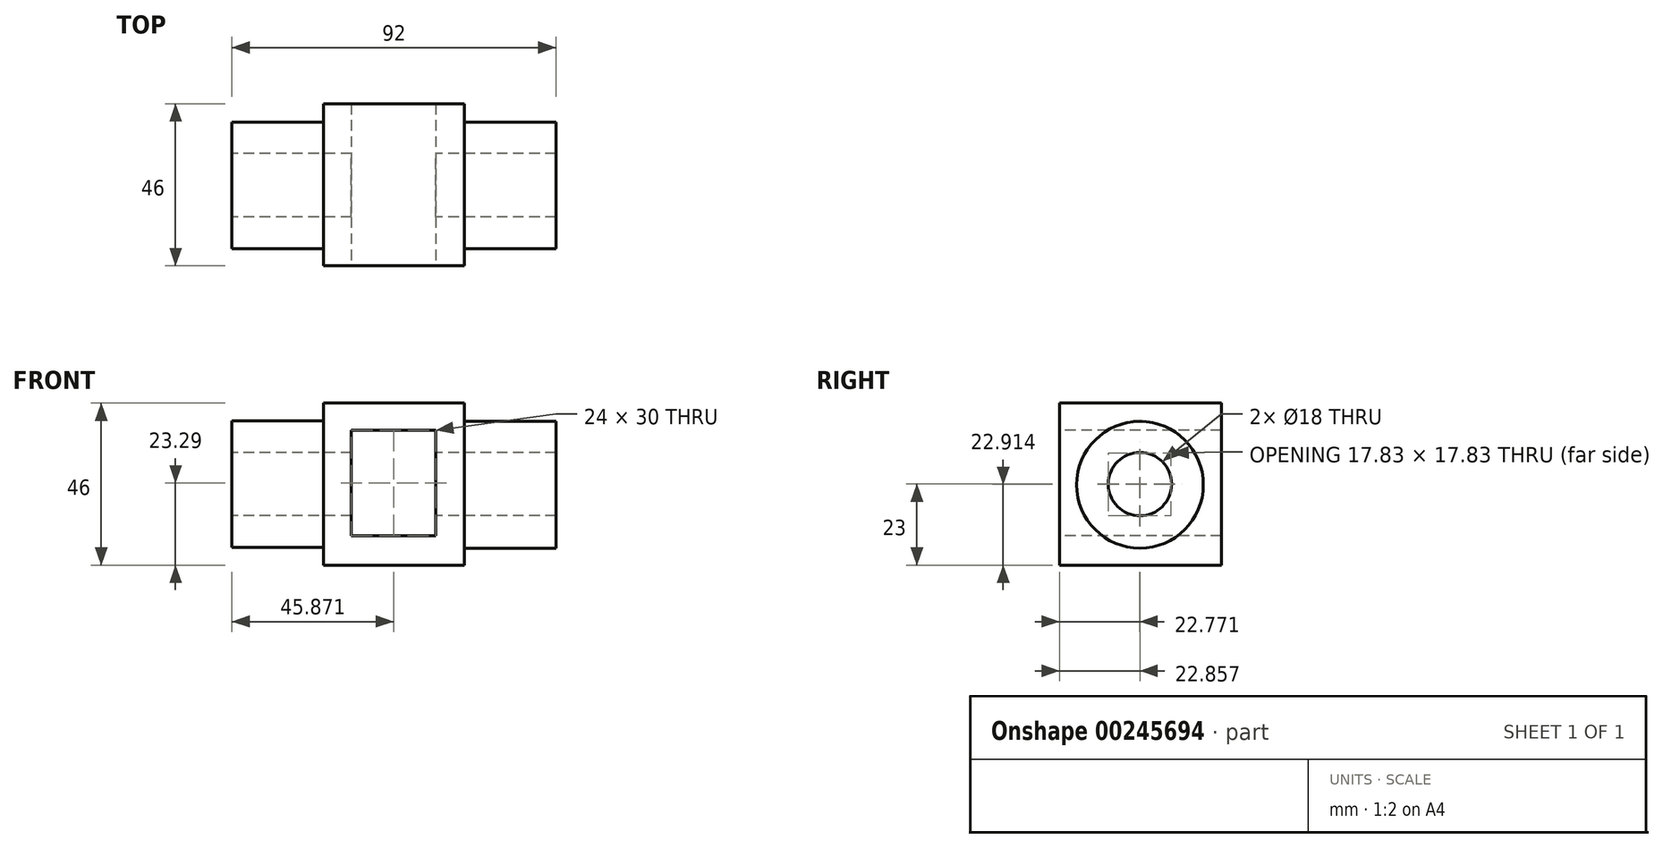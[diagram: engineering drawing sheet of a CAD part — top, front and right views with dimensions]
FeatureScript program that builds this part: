
annotation { "Feature Type Name" : "Feature", "Feature Type Description" : "" }
export const myFeature = defineFeature(function(context is Context, id is Id, definition is map)
    precondition{}
    {
        {
            var Q0;
            Q0=qCreatedBy(makeId("Top.planeOp"),FACE);
            var sketch = newSketch(context, id + "F0", { "sketchPlane" : qUnion([Q0])});
            skLineSegment(sketch, "E0.bottom", {"start": v(-3.43, 8.34) * mm, "end": v(36.57, 8.34) * mm});
            skLineSegment(sketch, "E0.top", {"start": v(-3.43, -37.66) * mm, "end": v(36.57, -37.66) * mm});
            skLineSegment(sketch, "E0.left", {"start": v(-3.43, 8.34) * mm, "end": v(-3.43, -37.66) * mm});
            skLineSegment(sketch, "E0.right", {"start": v(36.57, 8.34) * mm, "end": v(36.57, -37.66) * mm});
            skSolve(sketch);
        }
        {
            var Q0;
            Q0=makeQuery(id+"F0.imprint","IMPRINT",FACE,{"disambiguationData":[TD([[makeQuery(id+"F0.imprint","IMPRINT",EDGE,{"derivedFrom":sQuery(id+"F0.wireOp",EDGE,"E0.bottom")}),-1.0]])]});
            extrude(context, id + "F1", {"entities" : qUnion([Q0]), "depth" : 46 * mm});
        }
        {
            var Q0;
            Q0=makeQuery(id+"F1.opExtrude","SWEPT_FACE",FACE,{"disambiguationData":[OSD([sQuery(id+"F0.wireOp",EDGE,"E0.top")])]});
            var sketch = newSketch(context, id + "F2", { "sketchPlane" : qUnion([Q0])});
            skLineSegment(sketch, "E1.bottom", {"start": v(-3.43, 0) * mm, "end": v(4.57, 0) * mm});
            skLineSegment(sketch, "E1.top", {"start": v(-3.43, 8) * mm, "end": v(4.57, 8) * mm});
            skLineSegment(sketch, "E1.left", {"start": v(-3.43, 0) * mm, "end": v(-3.43, 8) * mm});
            skLineSegment(sketch, "E1.right", {"start": v(4.57, 0) * mm, "end": v(4.57, 8) * mm});
            skLineSegment(sketch, "E2.bottom", {"start": v(36.57, 46) * mm, "end": v(28.57, 46) * mm});
            skLineSegment(sketch, "E2.top", {"start": v(36.57, 38) * mm, "end": v(28.57, 38) * mm});
            skLineSegment(sketch, "E2.left", {"start": v(36.57, 46) * mm, "end": v(36.57, 38) * mm});
            skLineSegment(sketch, "E2.right", {"start": v(28.57, 46) * mm, "end": v(28.57, 38) * mm});
            skSolve(sketch);
        }
        {
            var Q0;
            {var subQ7=sQuery(id+"F2.wireOp",EDGE,"E1.top");Q0=makeQuery(id+"F2.imprint","IMPRINT",FACE,{"disambiguationData":[TD([[makeQuery(id+"F2.imprint","IMPRINT",EDGE,{"derivedFrom":subQ7}),1.0]])]});}
            var sketch = newSketch(context, id + "F3", { "sketchPlane" : qUnion([Q0])});
            skLineSegment(sketch, "E3.bottom", {"start": v(4.44, 8.29) * mm, "end": v(28.44, 8.29) * mm});
            skLineSegment(sketch, "E3.top", {"start": v(4.44, 38.29) * mm, "end": v(28.44, 38.29) * mm});
            skLineSegment(sketch, "E3.left", {"start": v(4.44, 8.29) * mm, "end": v(4.44, 38.29) * mm});
            skLineSegment(sketch, "E3.right", {"start": v(28.44, 8.29) * mm, "end": v(28.44, 38.29) * mm});
            skSolve(sketch);
        }
        {
            var Q0;
            Q0=makeQuery(id+"F3.imprint","IMPRINT",FACE,{"disambiguationData":[TD([[makeQuery(id+"F3.imprint","IMPRINT",EDGE,{"derivedFrom":sQuery(id+"F3.wireOp",EDGE,"E3.bottom")}),1.0]])]});
            extrude(context, id + "F4", {"entities" : qUnion([Q0]), "operationType" : NewBodyOperationType.REMOVE, "oppositeDirection" : true, "depth" : 46 * mm});
        }
        {
            var Q0;
            Q0=makeQuery(id+"F1.opExtrude","SWEPT_FACE",FACE,{"disambiguationData":[OSD([sQuery(id+"F0.wireOp",EDGE,"E0.right")])]});
            var sketch = newSketch(context, id + "F5", { "sketchPlane" : qUnion([Q0])});
            skCircle(sketch, "E4", {"center": v(-14.8, 22.8) * mm, "radius": 18 * mm});
            skSolve(sketch);
        }
        {
            var Q0;
            Q0=makeQuery(id+"F5.imprint","IMPRINT",FACE,{"disambiguationData":[TD([[makeQuery(id+"F5.imprint","IMPRINT",EDGE,{"derivedFrom":sQuery(id+"F5.wireOp",EDGE,"E4")}),1.0]])]});
            extrude(context, id + "F6", {"entities" : qUnion([Q0]), "operationType" : NewBodyOperationType.ADD, "depth" : 26 * mm});
        }
        {
            var Q0;
            Q0=makeQuery(id+"F1.opExtrude","SWEPT_FACE",FACE,{"disambiguationData":[OSD([sQuery(id+"F0.wireOp",EDGE,"E0.left")])]});
            var sketch = newSketch(context, id + "F7", { "sketchPlane" : qUnion([Q0])});
            skCircle(sketch, "E5", {"center": v(14.8, 23) * mm, "radius": 18 * mm});
            skPoint(sketch, "E5.centerSnap0", {"position": v(-8.34, 23) * mm});
            skSolve(sketch);
        }
        {
            var Q0;
            Q0=makeQuery(id+"F7.imprint","IMPRINT",FACE,{"disambiguationData":[TD([[makeQuery(id+"F7.imprint","IMPRINT",EDGE,{"derivedFrom":sQuery(id+"F7.wireOp",EDGE,"E5")}),1.0]])]});
            extrude(context, id + "F8", {"entities" : qUnion([Q0]), "operationType" : NewBodyOperationType.ADD, "depth" : 26 * mm});
        }
        {
            var Q0;
            Q0=makeQuery(id+"F8.opExtrude","CAP_FACE",FACE,{"disambiguationData":[OSD([sQuery(id+"F7.wireOp",EDGE,"E5")])],"isStart":false});
            var sketch = newSketch(context, id + "F9", { "sketchPlane" : qUnion([Q0])});
            skCircle(sketch, "E6", {"center": v(14.8, 23) * mm, "radius": 9 * mm});
            skSolve(sketch);
        }
        {
            var Q0;
            Q0=makeQuery(id+"F9.imprint","IMPRINT",FACE,{"disambiguationData":[TD([[makeQuery(id+"F9.imprint","IMPRINT",EDGE,{"derivedFrom":sQuery(id+"F9.wireOp",EDGE,"E6")}),1.0]])]});
            extrude(context, id + "F10", {"entities" : qUnion([Q0]), "operationType" : NewBodyOperationType.REMOVE, "oppositeDirection" : true, "depth" : 92 * mm});
        }
    });
